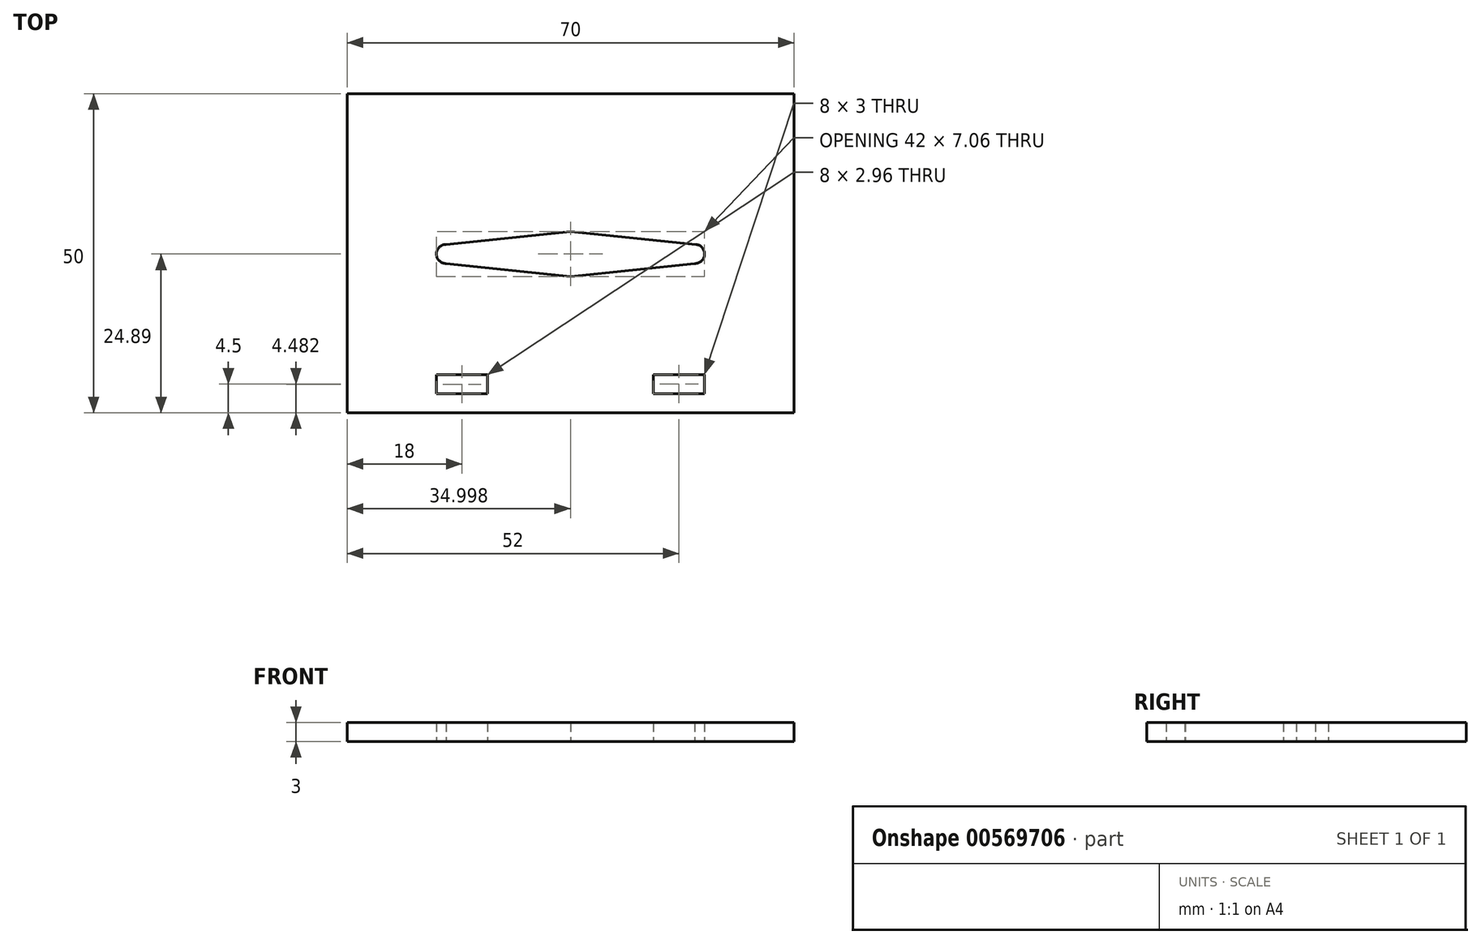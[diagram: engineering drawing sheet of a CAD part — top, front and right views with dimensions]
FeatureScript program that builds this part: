
annotation { "Feature Type Name" : "Feature", "Feature Type Description" : "" }
export const myFeature = defineFeature(function(context is Context, id is Id, definition is map)
    precondition{}
    {
        {
            var Q0;
            Q0=qCreatedBy(makeId("Top.planeOp"),FACE);
            var sketch = newSketch(context, id + "F0", { "sketchPlane" : qUnion([Q0])});
            skLineSegment(sketch, "E0", {"start": v(-35, 25.11) * mm, "end": v(35, 25.11) * mm});
            skLineSegment(sketch, "E1", {"start": v(35, 25.11) * mm, "end": v(35, -24.89) * mm});
            skLineSegment(sketch, "E2", {"start": v(35, -24.89) * mm, "end": v(-35, -24.89) * mm});
            skLineSegment(sketch, "E3", {"start": v(-35, -24.89) * mm, "end": v(-35, 25.11) * mm});
            skLineSegment(sketch, "E4", {"start": v(-21, -18.93) * mm, "end": v(-13, -18.93) * mm});
            skLineSegment(sketch, "E5", {"start": v(-13, -18.93) * mm, "end": v(-13, -21.89) * mm});
            skLineSegment(sketch, "E6", {"start": v(-13, -21.89) * mm, "end": v(-21, -21.89) * mm});
            skLineSegment(sketch, "E7", {"start": v(-21, -21.89) * mm, "end": v(-21, -18.93) * mm});
            skLineSegment(sketch, "E8.bottom", {"start": v(13, -18.89) * mm, "end": v(21, -18.89) * mm});
            skLineSegment(sketch, "E8.top", {"start": v(13, -21.89) * mm, "end": v(21, -21.89) * mm});
            skLineSegment(sketch, "E8.left", {"start": v(13, -18.89) * mm, "end": v(13, -21.89) * mm});
            skLineSegment(sketch, "E8.right", {"start": v(21, -18.89) * mm, "end": v(21, -21.89) * mm});
            skCircle(sketch, "E9", {"center": v(-19.5, 0) * mm, "radius": 1.5 * mm});
            skCircle(sketch, "E10", {"center": v(19.5, 0) * mm, "radius": 1.5 * mm});
            skCircle(sketch, "E11", {"center": v(0, 0) * mm, "radius": 3.5 * mm});
            skLineSegment(sketch, "E12", {"start": v(-19.5, 1.5) * mm, "end": v(0, 3.53) * mm});
            skLineSegment(sketch, "E13", {"start": v(0, 3.53) * mm, "end": v(19.65, 1.5) * mm});
            skLineSegment(sketch, "E14.trimOffspring", {"start": v(-19.45, -1.5) * mm, "end": v(-19.5, -1.5) * mm});
            skPoint(sketch, "E15.start.orphan", {"position": v(0, -0.87) * mm});
            skLineSegment(sketch, "E16", {"start": v(-19.45, -1.5) * mm, "end": v(0, -3.53) * mm});
            skLineSegment(sketch, "E17", {"start": v(0, -3.53) * mm, "end": v(19.5, -1.5) * mm});
            skSolve(sketch);
        }
        {
            var Q0;
            Q0=makeQuery(id+"F0.imprint","IMPRINT",FACE,{"disambiguationData":[TD([[makeQuery(id+"F0.imprint","IMPRINT",EDGE,{"derivedFrom":sQuery(id+"F0.wireOp",EDGE,"E0")}),-1.0]])]});
            extrude(context, id + "F1", {"entities" : qUnion([Q0]), "depth" : 3 * mm, "offsetDistance" : 25 * mm});
        }
    });
